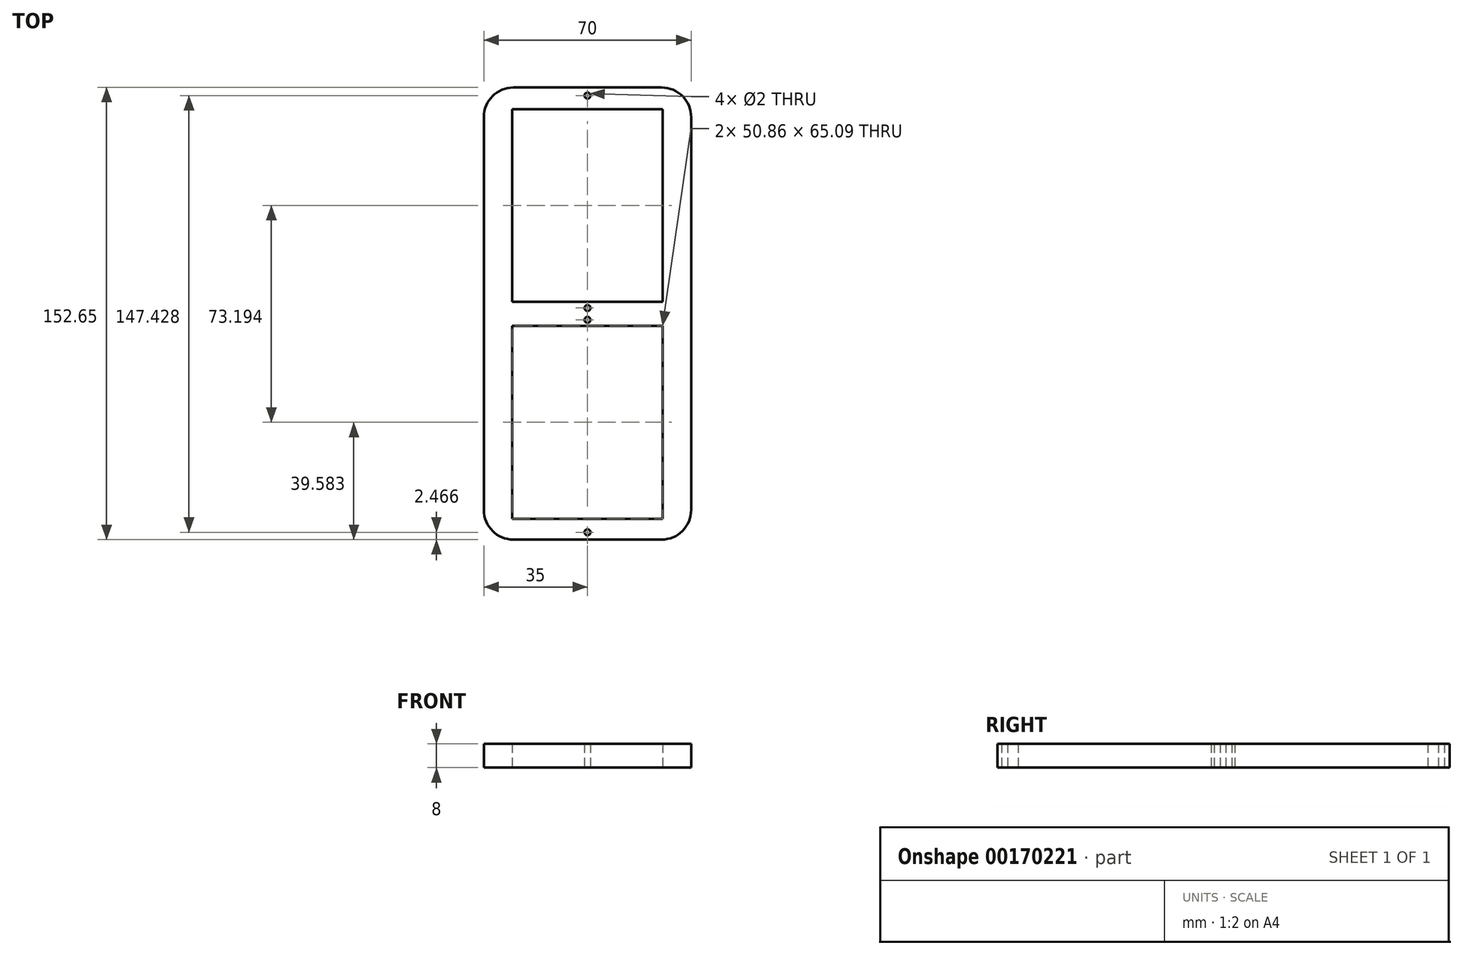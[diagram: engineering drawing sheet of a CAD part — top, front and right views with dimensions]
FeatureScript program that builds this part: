
annotation { "Feature Type Name" : "Feature", "Feature Type Description" : "" }
export const myFeature = defineFeature(function(context is Context, id is Id, definition is map)
    precondition{}
    {
        {
            var Q0;
            Q0=qCreatedBy(makeId("Top.planeOp"),FACE);
            var sketch = newSketch(context, id + "F0", { "sketchPlane" : qUnion([Q0])});
            skLineSegment(sketch, "E0.bottom", {"start": v(-35, 76.47) * mm, "end": v(35, 76.47) * mm});
            skLineSegment(sketch, "E0.top", {"start": v(-35, -76.18) * mm, "end": v(35, -76.18) * mm});
            skLineSegment(sketch, "E0.left", {"start": v(-35, 76.47) * mm, "end": v(-35, -76.18) * mm});
            skLineSegment(sketch, "E0.right", {"start": v(35, 76.47) * mm, "end": v(35, -76.18) * mm});
            skPoint(sketch, "E1.middle", {"position": v(0, 36.6) * mm});
            skPoint(sketch, "E2", {"position": v(0, 73.71) * mm});
            skPoint(sketch, "E3.MirrorP", {"position": v(0, -73.71) * mm});
            skLineSegment(sketch, "E4.bottom", {"start": v(-25.43, 69.14) * mm, "end": v(25.43, 69.14) * mm});
            skLineSegment(sketch, "E4.left", {"start": v(-25.43, 69.14) * mm, "end": v(-25.43, 4.05) * mm});
            skLineSegment(sketch, "E4.right", {"start": v(25.43, 69.14) * mm, "end": v(25.43, 4.05) * mm});
            skLineSegment(sketch, "E5.MirrorCS", {"start": v(-25.43, -69.14) * mm, "end": v(-25.43, -4.05) * mm});
            skLineSegment(sketch, "E6.MirrorCS", {"start": v(-25.43, -4.05) * mm, "end": v(25.43, -4.05) * mm});
            skLineSegment(sketch, "E7.MirrorCS", {"start": v(25.43, -69.14) * mm, "end": v(25.43, -4.05) * mm});
            skLineSegment(sketch, "E8.MirrorCS", {"start": v(-25.43, -69.14) * mm, "end": v(25.43, -69.14) * mm});
            skPoint(sketch, "E9", {"position": v(0, -4.05) * mm});
            skLineSegment(sketch, "E10.MirrorCS", {"start": v(-25.43, 4.05) * mm, "end": v(25.43, 4.05) * mm});
            skPoint(sketch, "E11", {"position": v(0, 2) * mm});
            skPoint(sketch, "E12", {"position": v(0, -2) * mm});
            skSolve(sketch);
        }
        {
            var Q0;
            Q0=makeQuery(id+"F0.imprint","IMPRINT",FACE,{"disambiguationData":[TD([[makeQuery(id+"F0.imprint","IMPRINT",EDGE,{"derivedFrom":sQuery(id+"F0.wireOp",EDGE,"E0.bottom")}),-1.0]])]});
            extrude(context, id + "F1", {"entities" : qUnion([Q0]), "depth" : 8 * mm});
        }
        {
            var Q0;
            Q0=sQuery(id+"F0.wireOp",VERTEX,"E11");
            var Q1;
            Q1=sQuery(id+"F0.wireOp",VERTEX,"E12");
            var Q2;
            Q2=sQuery(id+"F0.wireOp",VERTEX,"E2");
            var Q3;
            Q3=sQuery(id+"F0.wireOp",VERTEX,"E3.MirrorP");
            var Q4;
            Q4=makeQuery(id+"F1.opExtrude","SWEPT_BODY",BODY,{"disambiguationData":[OSD([sQuery(id+"F0.wireOp",EDGE,"E0.bottom"),sQuery(id+"F0.wireOp",EDGE,"E0.top"),sQuery(id+"F0.wireOp",EDGE,"E0.left"),sQuery(id+"F0.wireOp",EDGE,"E0.right"),sQuery(id+"F0.wireOp",EDGE,"E4.bottom"),sQuery(id+"F0.wireOp",EDGE,"E4.top"),sQuery(id+"F0.wireOp",EDGE,"E4.left"),sQuery(id+"F0.wireOp",EDGE,"E4.right"),sQuery(id+"F0.wireOp",EDGE,"E5.MirrorCS"),sQuery(id+"F0.wireOp",EDGE,"E6.MirrorCS"),sQuery(id+"F0.wireOp",EDGE,"E7.MirrorCS"),sQuery(id+"F0.wireOp",EDGE,"E8.MirrorCS")])]});
            hole(context, id + "F2", {"style" : HoleStyle.SIMPLE, "endStyle" : HoleEndStyle.BLIND, "oppositeDirection" : true, "holeDiameter" : 2 * mm, "holeDepth" : 50 * mm, "startFromSketch" : true, "locations" : qUnion([Q0, Q1, Q2, Q3]), "scope" : qUnion([Q4])});
        }
        {
            var Q0;
            Q0=makeQuery(id+"F1.opExtrude","SWEPT_EDGE",EDGE,{"disambiguationData":[OSD([sQuery(id+"F0.wireOp",EDGE,"E0.bottom"),sQuery(id+"F0.wireOp",EDGE,"E0.left")])]});
            var Q1;
            Q1=makeQuery(id+"F1.opExtrude","SWEPT_EDGE",EDGE,{"disambiguationData":[OSD([sQuery(id+"F0.wireOp",EDGE,"E0.bottom"),sQuery(id+"F0.wireOp",EDGE,"E0.right")])]});
            var Q2;
            Q2=makeQuery(id+"F1.opExtrude","SWEPT_EDGE",EDGE,{"disambiguationData":[OSD([sQuery(id+"F0.wireOp",EDGE,"E0.top"),sQuery(id+"F0.wireOp",EDGE,"E0.left")])]});
            var Q3;
            Q3=makeQuery(id+"F1.opExtrude","SWEPT_EDGE",EDGE,{"disambiguationData":[OSD([sQuery(id+"F0.wireOp",EDGE,"E0.top"),sQuery(id+"F0.wireOp",EDGE,"E0.right")])]});
            fillet(context, id + "F3", {"entities" : qUnion([Q0, Q1, Q2, Q3]), "radius" : 10 * mm, "tangentPropagation" : true, "allowEdgeOverflow" : false});
        }
    });
